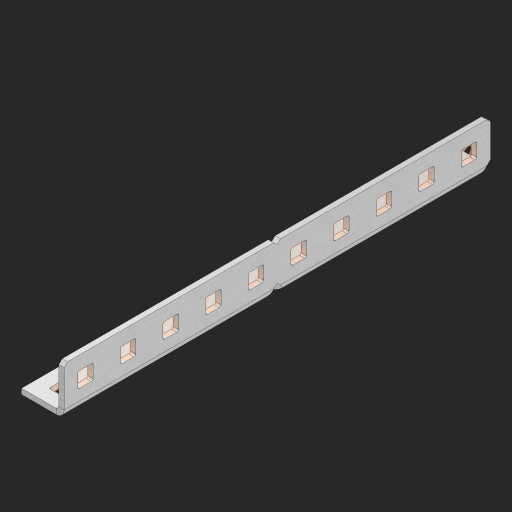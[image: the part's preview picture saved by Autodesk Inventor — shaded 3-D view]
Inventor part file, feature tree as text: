
AUTODESK INVENTOR PART (.ipt)
format: ipt  version: 2023 (Build 270158000, 158)  size: 505,344 bytes
history: native  units: in
note: dims shown in document units (in); Inventor stores cm internally (conversion verified against a paired STEP export)
features: other x25, extrude x19, sheet_metal_op x10, sketch x8, mirror x1, pattern_linear x1, chamfer x1
ambient origin geometry x8: Origin, YZ Plane, XZ Plane, XY Plane, X Axis, Y Axis, Z Axis, Center Point
bodies: Solid1 (feature_tree), Body (feature_tree)
feature tree (65):
  other  "Flange Pattern Plane"
  sheet_metal_op  "Flange Pattern"
  sheet_metal_op  "Body Pattern"
  other  "Arc Length"
  mirror  "Notch Mirror"
  pattern_linear  "Notch Pattern"  Spacing1=0.25in  [1 undecoded]
  chamfer  "End Chamfer"
  extrude  "Half Cut"  Depth=0.0625in
  sketch  "Sketch1"  dims[d0=1.5in]
  other  "Plate1"
  sketch  "Sketch2"  dims[d1=5.0in]
  other  "Plate2"
  sheet_metal_op  "Bend1"
  sheet_metal_op  "Corner1"
  sketch  "Sketch3"  dims[d2=0.0625in]
  other  "Flange Pattern Sketch"
  sketch  "Sketch7"  dims[d3=0.0625in]
  other  "Srf1"
  other  "Srf2"
  sketch  "Sketch8"  dims[d4=0.0312in]
  sketch  "Sketch9"  dims[d5=0.125in]
  other  "Srf91"
  sheet_metal_op  "Body Pattern Sketch"
  other  "Srf92"
  sketch  "Sketch13"  dims[d6=0.0625in]
  sketch  "Sketch14"  dims[d7=0.5in d8=90.0deg d9=0.0312in d10=0.25in d11=0.0625in d12=0.0625in d16=0.182in d17=0.02in d18=0.0625in d19=0.0in d20=0.25in d21=0.25in d46=0.172in d47=1.0in d48=0.0in d49=0.182in d50=0.02in d51=0.25in d52=0.25in d53=0.0625in d54=0.0in d55=0.172in d56=1.0in d57=0.0in d60=3.937in d62=0.5in d63=0.3937in d65=0.5in d85=0.1473in d86=0.1782in d88=0.04in d89=0.0625in d90=0.0in d91=0.04in d92=0.0491in d95=2.5in d96=0.04in d97=0.25in d98=45.0deg d101=0.0in d102=2.497in d131=0.5in d132=3.937in d134=0.5in d139=0.5in]
  other  "Srf856"
  other  "Srf1310"
  other  "Srf1311"
  other  "Srf1312"
  other  "Srf1376"
  other  "Srf1377"
  other  "Srf1728"
  other  "Srf1755"
  other  "Srf1878"
  other  "Srf1879"
  other  "Srf1880"
  other  "Srf1881"
  other  "Srf1942"
  other  "Srf1943"
  other  "Srf1944"
  other  "Srf1945"
  sheet_metal_op  "Flange Stamp"
  sheet_metal_op  "Flange Circle"
  sheet_metal_op  "Body Stamp"
  sheet_metal_op  "Body Circle"
  sheet_metal_op  "Notch"
  extrude  "ExtrusionSrf2"  Depth=0.0625in
  extrude  "ExtrusionSrf92"  Depth=0.5in
  extrude  "ExtrusionSrf856"  Depth=0.02in
  extrude  "ExtrusionSrf1310"  Depth=0.0625in
  extrude  "ExtrusionSrf1311"  TaperAngle=0.0deg  [1 undecoded]
  extrude  "ExtrusionSrf1312"  Depth=0.5in
  extrude  "ExtrusionSrf1376"  Depth=0.5in
  extrude  "ExtrusionSrf1377"  Depth=0.5in
  extrude  "ExtrusionSrf1728"  Depth=0.5in TaperAngle=0.0deg
  extrude  "ExtrusionSrf1755"  Depth=0.5in
  extrude  "ExtrusionSrf1878"  Depth=0.02in
  extrude  "ExtrusionSrf1879"  Depth=0.5in
  extrude  "ExtrusionSrf1880"  Depth=0.5in
  extrude  "ExtrusionSrf1881"  Depth=0.0625in
  extrude  "ExtrusionSrf1942"  TaperAngle=0.0deg  [1 undecoded]
  extrude  "ExtrusionSrf1943"  Depth=0.5in
  extrude  "ExtrusionSrf1944"  Depth=0.5in TaperAngle=0.0deg
  extrude  "ExtrusionSrf1945"  Depth=0.5in
note: 3 required parameter values undecoded (feature->parameter linkage not recoverable at this tier; creation-order binding heuristic only, values carry confidence <= 0.55)
